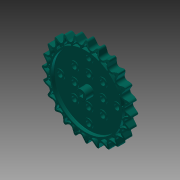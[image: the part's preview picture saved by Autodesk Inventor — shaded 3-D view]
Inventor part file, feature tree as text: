
AUTODESK INVENTOR PART (.ipt)
format: ipt  version: 2013 (Build 170138000, 138)  size: 1,801,216 bytes
history: native  units: in
note: dims shown in document units (in); Inventor stores cm internally (conversion verified against a paired STEP export)
features: sketch x7, extrude x7, fillet x2, revolve x1, pattern_circular x1, hole x1, mirror x1, projected_geometry x1, other x1
ambient origin geometry x8: Origin, YZ Plane, XZ Plane, XY Plane, X Axis, Y Axis, Z Axis, Center Point
bodies: Solid1 (feature_tree)
feature tree (22):
  sketch  "Sketch1"  dims[d0=0.3in d1=0.0in d2=2.441in]
  extrude  "Extrusion1"  Depth=2.441in
  extrude  "Extrusion2"  Depth=0.354in
  extrude  "Extrusion3"  Depth=0.029in
  revolve  "Revolution1"  Angle=90.0deg
  extrude  "Extrusion4"  Depth=0.012in
  fillet  "Fillet1"  Radius=0.012in
  pattern_circular  "Circular Pattern1"  Count=24 Angle=360.0deg
  fillet  "Fillet2"  Radius=0.315in
  sketch  "Sketch6"  dims[d18=0.175in d19=0.75in d20=0.375in d21=0.25in d22=0.5635in d23=1.0in d24=0.8108in d25=0.315in]
  hole  "Hole1"  [1 undecoded]
  extrude  "Extrusion5"  Depth=0.227in TaperAngle=0.0deg
  mirror  "Mirror1"
  extrude  "Extrusion6"  TaperAngle=0.0deg  [1 undecoded]
  sketch  "Sketch2"  dims[d3=0.111in d4=0.0in d5=0.354in]
  sketch  "Sketch3"  dims[d6=0.273in d7=0.0in d8=0.029in]
  sketch  "Sketch4"  dims[d9=0.165in d10=90.0deg]
  sketch  "Sketch5"  dims[d11=0.111in d12=0.0in d13=0.012in d14=0.012in d15=9.4488in d16=360.0deg]
  projected_geometry  "Projected Loop1"
  sketch  "Sketch7"  dims[d26=0.023in d27=0.0in d28=0.023in d29=0.0in d30=0.227in d31=0.0in d32=0.0in d33=0.0in]
  other  "Srf1"
  extrude  "ExtrusionSrf1"  TaperAngle=0.0deg  [1 undecoded]
note: 3 required parameter values undecoded (feature->parameter linkage not recoverable at this tier; creation-order binding heuristic only, values carry confidence <= 0.55)
